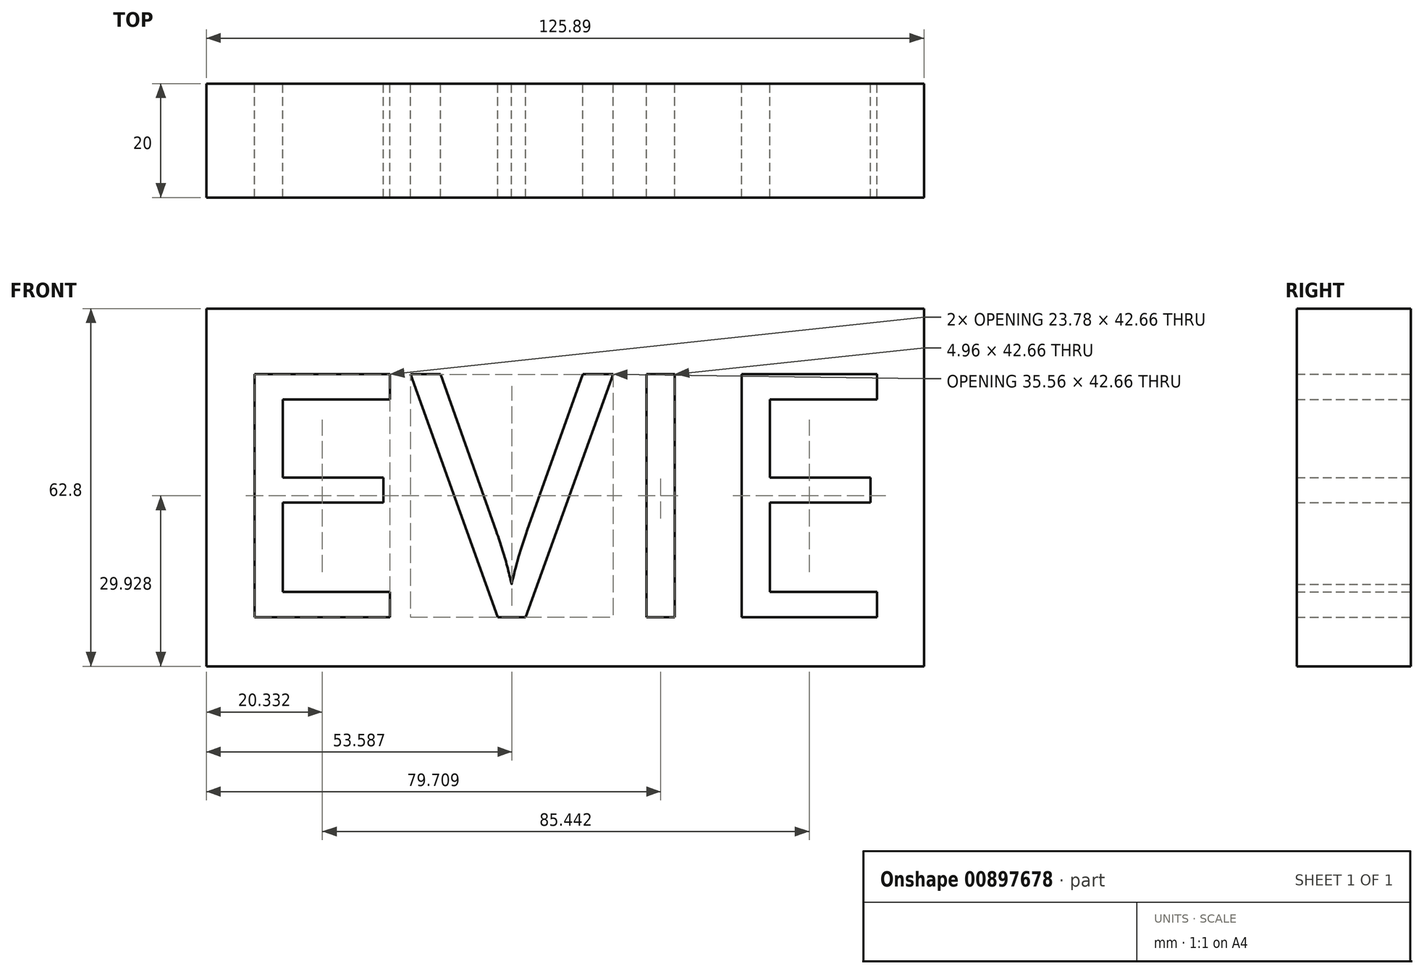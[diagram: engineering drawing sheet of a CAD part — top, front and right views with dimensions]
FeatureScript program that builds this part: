
annotation { "Feature Type Name" : "Feature", "Feature Type Description" : "" }
export const myFeature = defineFeature(function(context is Context, id is Id, definition is map)
    precondition{}
    {
        {
            var Q0;
            Q0=qCreatedBy(makeId("Front.planeOp"),FACE);
            var sketch = newSketch(context, id + "F0", { "sketchPlane" : qUnion([Q0])});
            skText(sketch, "E0", { "text": "EVIE", "fontName": "OpenSans-Regular.ttf"});
            skLineSegment(sketch, "E1.bottom", {"start": v(-60.94, 34.27) * mm, "end": v(64.95, 34.27) * mm});
            skLineSegment(sketch, "E1.top", {"start": v(-60.94, -28.53) * mm, "end": v(64.95, -28.53) * mm});
            skLineSegment(sketch, "E1.left", {"start": v(-60.94, 34.27) * mm, "end": v(-60.94, -28.53) * mm});
            skLineSegment(sketch, "E1.right", {"start": v(64.95, 34.27) * mm, "end": v(64.95, -28.53) * mm});
            const initialGuessF0  = {"E0": [-0.05836, -0.01993, 1, 0, 0.04302]};
            skSetInitialGuess(sketch, initialGuessF0);
            skSolve(sketch);
        }
        {
            var Q0;
            Q0=makeQuery(id+"F0.imprint","IMPRINT",FACE,{"disambiguationData":[TD([[makeQuery(id+"F0.imprint","IMPRINT",EDGE,{"derivedFrom":sQuery(id+"F0.wireOp",EDGE,"E0.sketch_text.stroke-0")}),1.0]])]});
            extrude(context, id + "F1", {"entities" : qUnion([Q0]), "depth" : 20 * mm, "offsetDistance" : 25.4 * mm});
        }
    });
